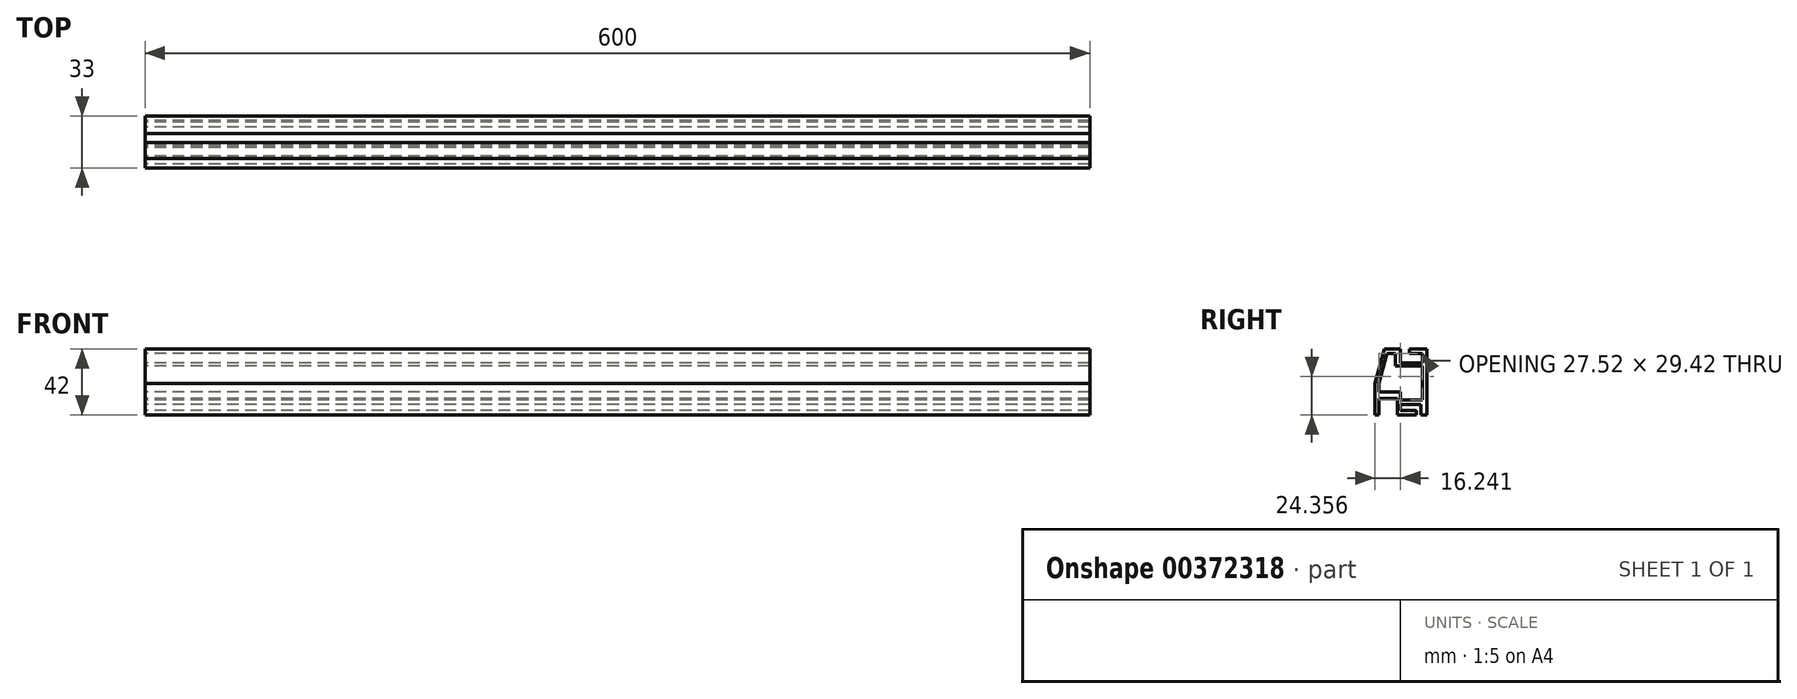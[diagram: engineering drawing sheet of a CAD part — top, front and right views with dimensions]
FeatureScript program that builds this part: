
annotation { "Feature Type Name" : "Feature", "Feature Type Description" : "" }
export const myFeature = defineFeature(function(context is Context, id is Id, definition is map)
    precondition{}
    {
        {
            var Q0;
            Q0=qCreatedBy(makeId("Right.planeOp"),FACE);
            var sketch = newSketch(context, id + "F0", { "sketchPlane" : qUnion([Q0])});
            skLineSegment(sketch, "E0.bottom", {"start": v(-13.4, 29.43) * mm, "end": v(-3.3, 29.43) * mm});
            skLineSegment(sketch, "E0.top", {"start": v(-19.4, -12.57) * mm, "end": v(-17.04, -12.57) * mm});
            skLineSegment(sketch, "E0.left", {"start": v(-19.4, 7.43) * mm, "end": v(-19.4, -12.57) * mm});
            skLineSegment(sketch, "E0.right", {"start": v(13.6, 29.43) * mm, "end": v(13.6, -12.57) * mm});
            skLineSegment(sketch, "E1", {"start": v(-19.4, 7.43) * mm, "end": v(-13.4, 29.43) * mm});
            skLineSegment(sketch, "E2", {"start": v(2.45, 29.43) * mm, "end": v(2.45, 26.43) * mm});
            skLineSegment(sketch, "E3", {"start": v(2.45, 26.43) * mm, "end": v(10.6, 26.43) * mm});
            skLineSegment(sketch, "E4", {"start": v(10.6, 26.43) * mm, "end": v(10.6, 20.56) * mm});
            skLineSegment(sketch, "E5", {"start": v(10.6, 20.56) * mm, "end": v(-3.3, 20.56) * mm});
            skLineSegment(sketch, "E6", {"start": v(-3.3, 20.56) * mm, "end": v(-3.3, 29.43) * mm});
            skLineSegment(sketch, "E7", {"start": v(-11.74, 26.5) * mm, "end": v(-6.52, 26.5) * mm});
            skLineSegment(sketch, "E8", {"start": v(-6.52, 26.5) * mm, "end": v(-6.52, 18.5) * mm});
            skLineSegment(sketch, "E9", {"start": v(-6.52, 18.5) * mm, "end": v(10.6, 18.5) * mm});
            skLineSegment(sketch, "E10", {"start": v(10.6, 18.5) * mm, "end": v(10.6, -2.93) * mm});
            skLineSegment(sketch, "E11", {"start": v(10.6, -2.93) * mm, "end": v(-3.24, -2.93) * mm});
            skLineSegment(sketch, "E12", {"start": v(-3.24, -2.93) * mm, "end": v(-3.24, 2.06) * mm});
            skLineSegment(sketch, "E13", {"start": v(-3.24, 2.06) * mm, "end": v(-16.92, 2.06) * mm});
            skLineSegment(sketch, "E14", {"start": v(-16.92, 2.06) * mm, "end": v(-16.92, 7.5) * mm});
            skLineSegment(sketch, "E15", {"start": v(-16.92, 7.5) * mm, "end": v(-11.74, 26.5) * mm});
            skLineSegment(sketch, "E16", {"start": v(-17.04, -12.57) * mm, "end": v(-17.04, -2) * mm});
            skLineSegment(sketch, "E17", {"start": v(-17.04, -2) * mm, "end": v(-5.1, -2) * mm});
            skLineSegment(sketch, "E18", {"start": v(-5.1, -2) * mm, "end": v(-5.1, -12.57) * mm});
            skLineSegment(sketch, "E19", {"start": v(-3.24, -6.05) * mm, "end": v(-3.24, -9.76) * mm});
            skLineSegment(sketch, "E20", {"start": v(-3.24, -9.76) * mm, "end": v(6.72, -9.76) * mm});
            skLineSegment(sketch, "E21", {"start": v(6.72, -9.76) * mm, "end": v(6.72, -12.57) * mm});
            skLineSegment(sketch, "E22", {"start": v(-3.24, -6.05) * mm, "end": v(9.62, -6.05) * mm});
            skLineSegment(sketch, "E23", {"start": v(9.62, -6.05) * mm, "end": v(9.62, -12.57) * mm});
            skLineSegment(sketch, "E24.trimOffspring", {"start": v(2.45, 29.43) * mm, "end": v(13.6, 29.43) * mm});
            skLineSegment(sketch, "E25.trimOffspring", {"start": v(-5.1, -12.57) * mm, "end": v(6.72, -12.57) * mm});
            skLineSegment(sketch, "E26.trimOffspring", {"start": v(9.62, -12.57) * mm, "end": v(13.6, -12.57) * mm});
            skSolve(sketch);
        }
        {
            var Q0;
            Q0=makeQuery(id+"F0.imprint","IMPRINT",FACE,{"disambiguationData":[TD([[makeQuery(id+"F0.imprint","IMPRINT",EDGE,{"derivedFrom":sQuery(id+"F0.wireOp",EDGE,"E0.bottom")}),-1.0]])]});
            extrude(context, id + "F1", {"entities" : qUnion([Q0]), "depth" : 600 * mm, "offsetDistance" : 25 * mm});
        }
    });
